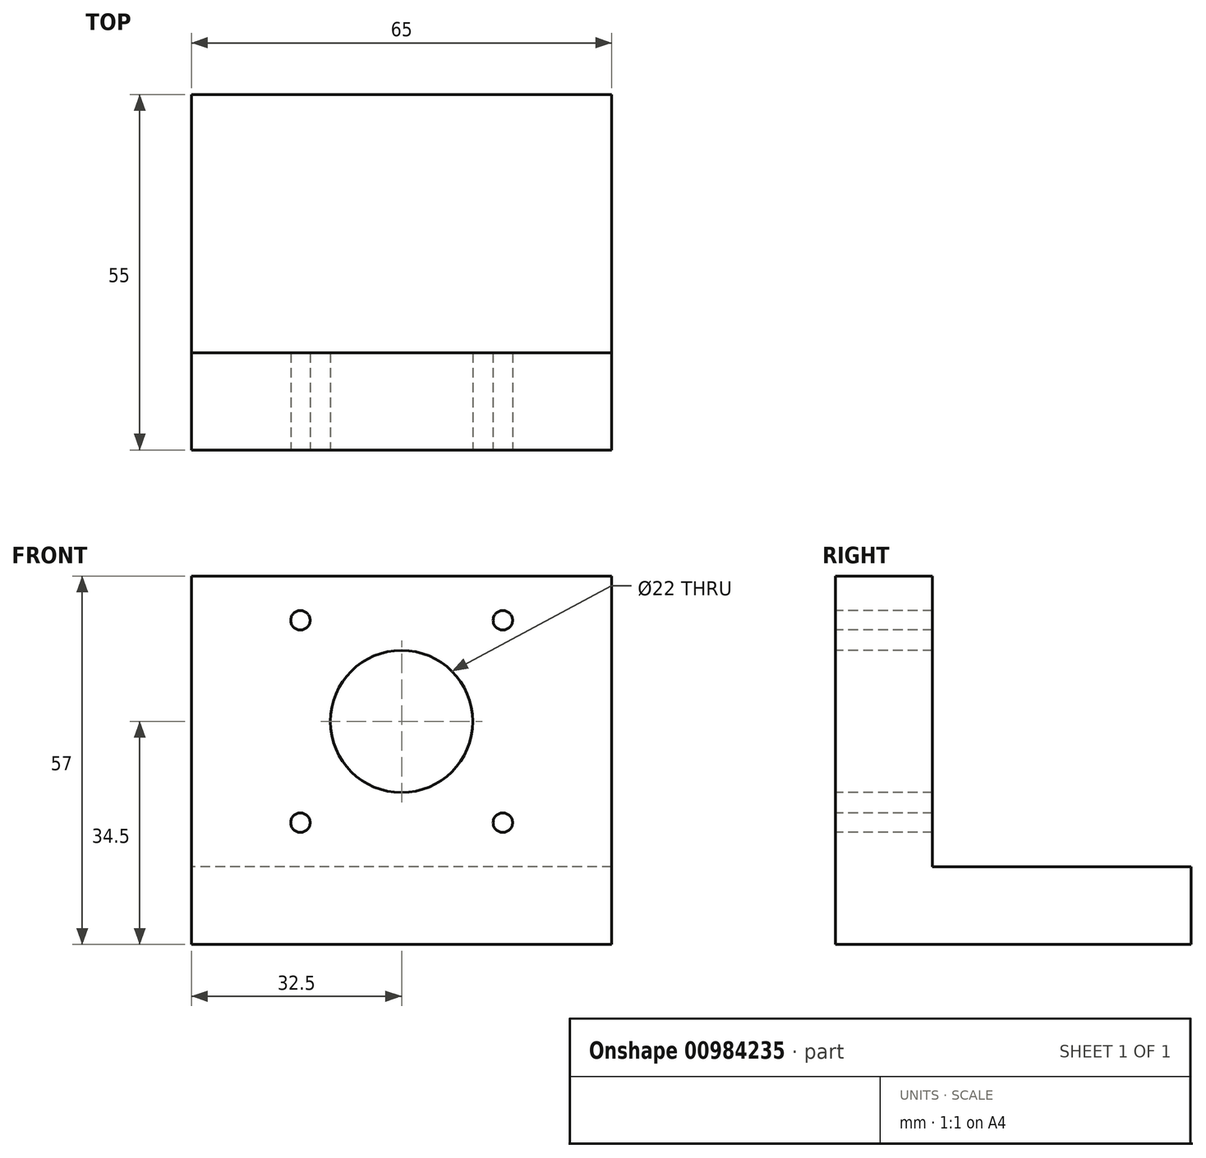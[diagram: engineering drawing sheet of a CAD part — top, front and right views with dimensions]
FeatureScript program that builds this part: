
annotation { "Feature Type Name" : "Feature", "Feature Type Description" : "" }
export const myFeature = defineFeature(function(context is Context, id is Id, definition is map)
    precondition{}
    {
        {
            var Q0;
            Q0=qCreatedBy(makeId("Front.planeOp"),FACE);
            var sketch = newSketch(context, id + "F0", { "sketchPlane" : qUnion([Q0])});
            skLineSegment(sketch, "E0.bottom", {"start": v(32.5, 28.5) * mm, "end": v(-32.5, 28.5) * mm});
            skLineSegment(sketch, "E0.top", {"start": v(32.5, -28.5) * mm, "end": v(-32.5, -28.5) * mm});
            skLineSegment(sketch, "E0.left", {"start": v(32.5, 28.5) * mm, "end": v(32.5, -28.5) * mm});
            skLineSegment(sketch, "E0.right", {"start": v(-32.5, 28.5) * mm, "end": v(-32.5, -28.5) * mm});
            skPoint(sketch, "E0.middle", {"position": v(0, 0) * mm});
            skSolve(sketch);
        }
        {
            var Q0;
            Q0=makeQuery(id+"F0.imprint","IMPRINT",FACE,{"disambiguationData":[TD([[makeQuery(id+"F0.imprint","IMPRINT",EDGE,{"derivedFrom":sQuery(id+"F0.wireOp",EDGE,"E0.bottom")}),1.0]])]});
            extrude(context, id + "F1", {"entities" : qUnion([Q0]), "oppositeDirection" : true, "depth" : 55 * mm, "offsetDistance" : 25 * mm});
        }
        {
            var Q0;
            Q0=makeQuery(id+"F1.opExtrude","CAP_FACE",FACE,{"disambiguationData":[OSD([sQuery(id+"F0.wireOp",EDGE,"E0.bottom"),sQuery(id+"F0.wireOp",EDGE,"E0.top"),sQuery(id+"F0.wireOp",EDGE,"E0.left"),sQuery(id+"F0.wireOp",EDGE,"E0.right")])],"isStart":false});
            var sketch = newSketch(context, id + "F2", { "sketchPlane" : qUnion([Q0])});
            skLineSegment(sketch, "E1.bottom", {"start": v(-32.5, 28.5) * mm, "end": v(32.5, 28.5) * mm});
            skLineSegment(sketch, "E1.top", {"start": v(-32.5, -16.5) * mm, "end": v(32.5, -16.5) * mm});
            skLineSegment(sketch, "E1.left", {"start": v(-32.5, 28.5) * mm, "end": v(-32.5, -16.5) * mm});
            skLineSegment(sketch, "E1.right", {"start": v(32.5, 28.5) * mm, "end": v(32.5, -16.5) * mm});
            skSolve(sketch);
        }
        {
            var Q0;
            Q0=makeQuery(id+"F2.imprint","IMPRINT",FACE,{"disambiguationData":[TD([[makeQuery(id+"F2.imprint","IMPRINT",EDGE,{"derivedFrom":sQuery(id+"F2.wireOp",EDGE,"E1.bottom")}),-1.0]])]});
            extrude(context, id + "F3", {"entities" : qUnion([Q0]), "operationType" : NewBodyOperationType.REMOVE, "oppositeDirection" : true, "depth" : 40 * mm, "offsetDistance" : 25 * mm});
        }
        {
            var Q0;
            Q0=makeQuery(id+"F1.opExtrude","CAP_FACE",FACE,{"disambiguationData":[OSD([sQuery(id+"F0.wireOp",EDGE,"E0.bottom"),sQuery(id+"F0.wireOp",EDGE,"E0.top"),sQuery(id+"F0.wireOp",EDGE,"E0.left"),sQuery(id+"F0.wireOp",EDGE,"E0.right")])],"isStart":true});
            var sketch = newSketch(context, id + "F4", { "sketchPlane" : qUnion([Q0])});
            skCircle(sketch, "E2", {"center": v(0, 6) * mm, "radius": 11 * mm});
            skSolve(sketch);
        }
        {
            var Q0;
            Q0=makeQuery(id+"F4.imprint","IMPRINT",FACE,{"disambiguationData":[TD([[makeQuery(id+"F4.imprint","IMPRINT",EDGE,{"derivedFrom":sQuery(id+"F4.wireOp",EDGE,"E2")}),1.0]])]});
            extrude(context, id + "F5", {"entities" : qUnion([Q0]), "operationType" : NewBodyOperationType.REMOVE, "oppositeDirection" : true, "depth" : 15 * mm, "offsetDistance" : 25 * mm});
        }
        {
            var Q0;
            Q0=makeQuery(id+"F1.opExtrude","CAP_FACE",FACE,{"disambiguationData":[OSD([sQuery(id+"F0.wireOp",EDGE,"E0.bottom"),sQuery(id+"F0.wireOp",EDGE,"E0.top"),sQuery(id+"F0.wireOp",EDGE,"E0.left"),sQuery(id+"F0.wireOp",EDGE,"E0.right")])],"isStart":true});
            var sketch = newSketch(context, id + "F6", { "sketchPlane" : qUnion([Q0])});
            skCircle(sketch, "E3", {"center": v(15.65, 21.65) * mm, "radius": 1.5 * mm});
            skSolve(sketch);
        }
        {
            var Q0;
            Q0=makeQuery(id+"F6.imprint","IMPRINT",FACE,{"disambiguationData":[TD([[makeQuery(id+"F6.imprint","IMPRINT",EDGE,{"derivedFrom":sQuery(id+"F6.wireOp",EDGE,"E3")}),-1.0]])]});
            var sketch = newSketch(context, id + "F7", { "sketchPlane" : qUnion([Q0])});
            skCircle(sketch, "E4", {"center": v(-15.65, 21.65) * mm, "radius": 1.5 * mm});
            skSolve(sketch);
        }
        {
            var Q0;
            Q0=makeQuery(id+"F6.imprint","IMPRINT",FACE,{"disambiguationData":[TD([[makeQuery(id+"F6.imprint","IMPRINT",EDGE,{"derivedFrom":sQuery(id+"F6.wireOp",EDGE,"E3")}),-1.0]])]});
            var sketch = newSketch(context, id + "F8", { "sketchPlane" : qUnion([Q0])});
            skCircle(sketch, "E5", {"center": v(15.65, -9.65) * mm, "radius": 1.5 * mm});
            skSolve(sketch);
        }
        {
            var Q0;
            Q0=makeQuery(id+"F6.imprint","IMPRINT",FACE,{"disambiguationData":[TD([[makeQuery(id+"F6.imprint","IMPRINT",EDGE,{"derivedFrom":sQuery(id+"F6.wireOp",EDGE,"E3")}),-1.0]])]});
            var sketch = newSketch(context, id + "F9", { "sketchPlane" : qUnion([Q0])});
            skCircle(sketch, "E6", {"center": v(-15.65, -9.65) * mm, "radius": 1.5 * mm});
            skSolve(sketch);
        }
        {
            var Q0;
            Q0=makeQuery(id+"F6.imprint","IMPRINT",FACE,{"disambiguationData":[TD([[makeQuery(id+"F6.imprint","IMPRINT",EDGE,{"derivedFrom":sQuery(id+"F6.wireOp",EDGE,"E3")}),1.0]])]});
            extrude(context, id + "F10", {"entities" : qUnion([Q0]), "operationType" : NewBodyOperationType.REMOVE, "oppositeDirection" : true, "depth" : 15 * mm, "offsetDistance" : 25 * mm});
        }
        {
            var Q0;
            Q0=makeQuery(id+"F7.imprint","IMPRINT",FACE,{"disambiguationData":[TD([[makeQuery(id+"F7.imprint","IMPRINT",EDGE,{"derivedFrom":sQuery(id+"F7.wireOp",EDGE,"E4")}),1.0]])]});
            extrude(context, id + "F11", {"entities" : qUnion([Q0]), "operationType" : NewBodyOperationType.REMOVE, "oppositeDirection" : true, "depth" : 15 * mm, "offsetDistance" : 25 * mm});
        }
        {
            var Q0;
            Q0=makeQuery(id+"F8.imprint","IMPRINT",FACE,{"disambiguationData":[TD([[makeQuery(id+"F8.imprint","IMPRINT",EDGE,{"derivedFrom":sQuery(id+"F8.wireOp",EDGE,"E5")}),1.0]])]});
            extrude(context, id + "F12", {"entities" : qUnion([Q0]), "operationType" : NewBodyOperationType.REMOVE, "oppositeDirection" : true, "depth" : 15 * mm, "offsetDistance" : 25 * mm});
        }
        {
            var Q0;
            Q0=makeQuery(id+"F9.imprint","IMPRINT",FACE,{"disambiguationData":[TD([[makeQuery(id+"F9.imprint","IMPRINT",EDGE,{"derivedFrom":sQuery(id+"F9.wireOp",EDGE,"E6")}),1.0]])]});
            extrude(context, id + "F13", {"entities" : qUnion([Q0]), "operationType" : NewBodyOperationType.REMOVE, "oppositeDirection" : true, "depth" : 15 * mm, "offsetDistance" : 25 * mm});
        }
    });
